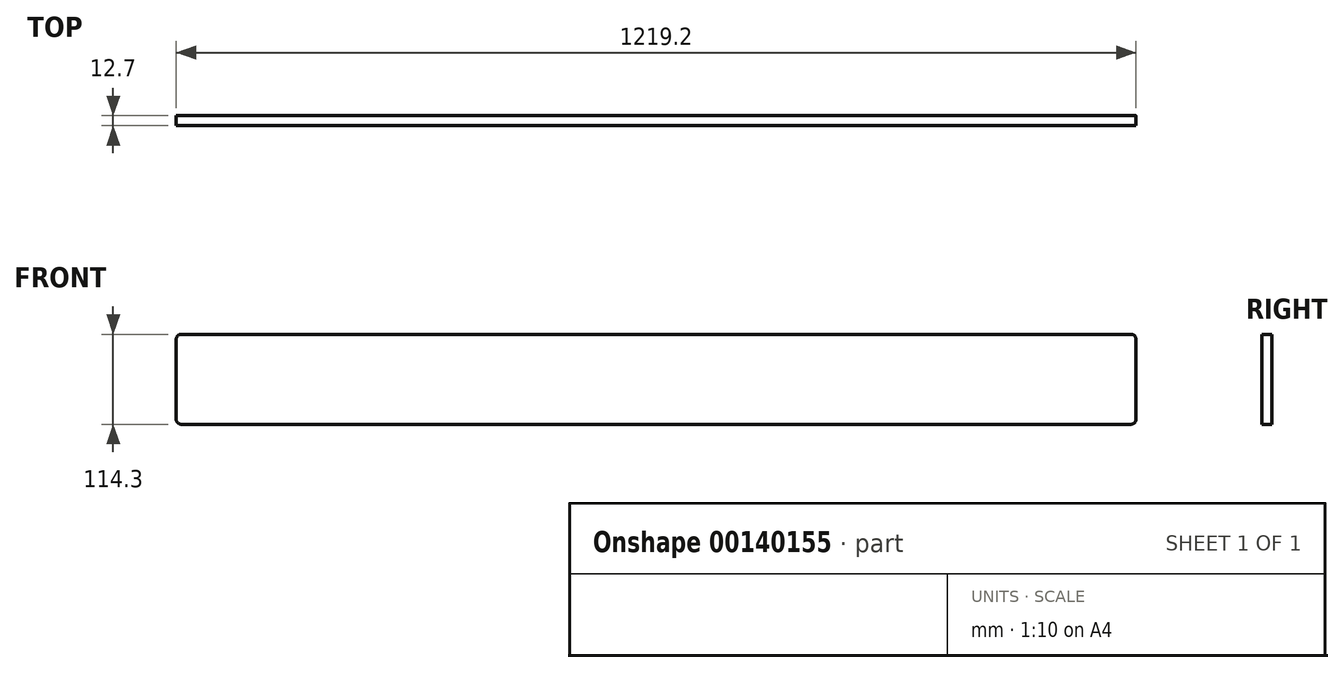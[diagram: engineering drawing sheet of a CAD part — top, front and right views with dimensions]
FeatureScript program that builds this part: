
annotation { "Feature Type Name" : "Feature", "Feature Type Description" : "" }
export const myFeature = defineFeature(function(context is Context, id is Id, definition is map)
    precondition{}
    {
        {
            var Q0;
            Q0=qCreatedBy(makeId("Front.planeOp"),FACE);
            var sketch = newSketch(context, id + "F0", { "sketchPlane" : qUnion([Q0])});
            skLineSegment(sketch, "E0", {"start": v(-609.6, 139.7) * mm, "end": v(-609.6, 38.1) * mm});
            skLineSegment(sketch, "E1", {"start": v(609.6, 139.7) * mm, "end": v(609.6, 38.1) * mm});
            skLineSegment(sketch, "E2.trimOffspring", {"start": v(603.25, 146.05) * mm, "end": v(-603.25, 146.05) * mm});
            skArc(sketch, "E3.filletArc", {"start": v(-603.25, 146.05) * mm, "mid": v(-607.74, 144.2) * mm, "end": v(-609.6, 139.7) * mm});
            skArc(sketch, "E4.filletArc", {"start": v(609.6, 139.7) * mm, "mid": v(607.74, 144.2) * mm, "end": v(603.25, 146.05) * mm});
            skLineSegment(sketch, "E5.trimOffspring", {"start": v(-603.25, 31.75) * mm, "end": v(603.25, 31.75) * mm});
            skArc(sketch, "E6.filletArc", {"start": v(603.25, 31.75) * mm, "mid": v(607.74, 33.6) * mm, "end": v(609.6, 38.1) * mm});
            skPoint(sketch, "E7.visualSharp", {"position": v(-609.6, 31.75) * mm});
            skArc(sketch, "E7.filletArc", {"start": v(-609.6, 38.1) * mm, "mid": v(-607.74, 33.6) * mm, "end": v(-603.25, 31.75) * mm});
            skSolve(sketch);
        }
        {
            var Q0;
            Q0=makeQuery(id+"F0.imprint","IMPRINT",FACE,{"disambiguationData":[TD([[makeQuery(id+"F0.imprint","IMPRINT",EDGE,{"derivedFrom":sQuery(id+"F0.wireOp",EDGE,"E0")}),1.0]])]});
            extrude(context, id + "F1", {"entities" : qUnion([Q0]), "depth" : 12.7 * mm});
        }
    });
